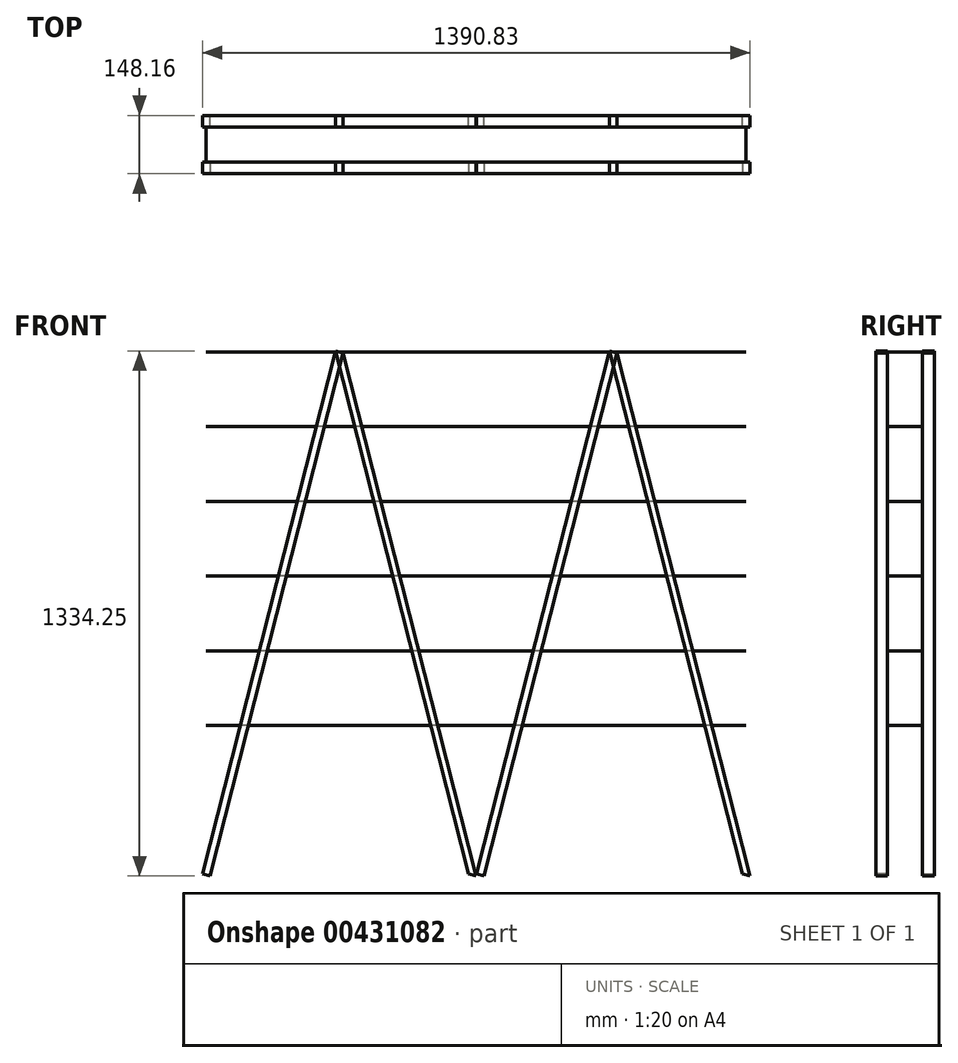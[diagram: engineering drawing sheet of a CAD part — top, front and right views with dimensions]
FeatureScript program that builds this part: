
annotation { "Feature Type Name" : "Feature", "Feature Type Description" : "" }
export const myFeature = defineFeature(function(context is Context, id is Id, definition is map)
    precondition{}
    {
        {
            var Q0;
            Q0=qCreatedBy(makeId("Front.planeOp"),FACE);
            var sketch = newSketch(context, id + "F0", { "sketchPlane" : qUnion([Q0])});
            skLineSegment(sketch, "E0", {"start": v(-53, 736.07) * mm, "end": v(-390.73, -593.3) * mm});
            skLineSegment(sketch, "E1", {"start": v(-53, 736.07) * mm, "end": v(284.75, -593.3) * mm});
            skLineSegment(sketch, "E2", {"start": v(284.75, -593.3) * mm, "end": v(305.39, -593.3) * mm});
            skLineSegment(sketch, "E3", {"start": v(305.39, -593.3) * mm, "end": v(643.13, 736.07) * mm});
            skLineSegment(sketch, "E4", {"start": v(643.13, 736.07) * mm, "end": v(980.87, -593.3) * mm});
            skLineSegment(sketch, "E5", {"start": v(-390.73, -593.3) * mm, "end": v(980.87, -593.3) * mm, "construction": true});
            skLineSegment(sketch, "E6", {"start": v(-390.73, -593.3) * mm, "end": v(-390.73, -645.75) * mm, "construction": true});
            skLineSegment(sketch, "E7", {"start": v(284.75, -593.3) * mm, "end": v(284.75, -645.75) * mm, "construction": true});
            skLineSegment(sketch, "E8", {"start": v(305.39, -593.3) * mm, "end": v(305.39, -645.75) * mm, "construction": true});
            skLineSegment(sketch, "E9", {"start": v(980.87, -593.3) * mm, "end": v(980.87, -645.75) * mm, "construction": true});
            skLineSegment(sketch, "E10", {"start": v(-390.73, -645.75) * mm, "end": v(284.75, -645.75) * mm, "construction": true});
            skLineSegment(sketch, "E11", {"start": v(305.39, -645.75) * mm, "end": v(980.87, -645.75) * mm, "construction": true});
            skLineSegment(sketch, "E12", {"start": v(980.87, 736.07) * mm, "end": v(-390.73, 736.07) * mm});
            skLineSegment(sketch, "E13", {"start": v(980.87, 546.16) * mm, "end": v(-390.73, 546.16) * mm});
            skLineSegment(sketch, "E14", {"start": v(980.87, 356.25) * mm, "end": v(-390.73, 356.25) * mm});
            skLineSegment(sketch, "E15", {"start": v(980.87, 166.34) * mm, "end": v(-390.73, 166.34) * mm});
            skLineSegment(sketch, "E16", {"start": v(980.87, -23.57) * mm, "end": v(-390.73, -23.57) * mm});
            skLineSegment(sketch, "E17", {"start": v(980.87, -213.48) * mm, "end": v(-390.73, -213.48) * mm});
            skLineSegment(sketch, "E18", {"start": v(643.13, 736.07) * mm, "end": v(643.13, 546.16) * mm, "construction": true});
            skLineSegment(sketch, "E19", {"start": v(643.13, 546.16) * mm, "end": v(643.13, 356.25) * mm, "construction": true});
            skLineSegment(sketch, "E20", {"start": v(643.13, 356.25) * mm, "end": v(643.13, 166.34) * mm, "construction": true});
            skLineSegment(sketch, "E21", {"start": v(643.13, 166.34) * mm, "end": v(643.13, -23.57) * mm, "construction": true});
            skLineSegment(sketch, "E22", {"start": v(643.13, -23.57) * mm, "end": v(643.13, -213.48) * mm, "construction": true});
            skLineSegment(sketch, "E23", {"start": v(980.87, -403.4) * mm, "end": v(-390.73, -403.4) * mm, "construction": true});
            skLineSegment(sketch, "E24", {"start": v(643.13, -213.48) * mm, "end": v(643.13, -403.4) * mm});
            skLineSegment(sketch, "E25", {"start": v(643.13, -403.4) * mm, "end": v(643.13, -593.3) * mm});
            skSolve(sketch);
        }
        {
            var Q0;
            Q0=sQuery(id+"F0.wireOp",EDGE,"E12");
            var Q1;
            Q1=sQuery(id+"F0.wireOp",EDGE,"E13");
            var Q2;
            Q2=sQuery(id+"F0.wireOp",EDGE,"E14");
            var Q3;
            Q3=sQuery(id+"F0.wireOp",EDGE,"E15");
            var Q4;
            Q4=sQuery(id+"F0.wireOp",EDGE,"E16");
            var Q5;
            Q5=sQuery(id+"F0.wireOp",EDGE,"E17");
            extrude(context, id + "F1", {"bodyType" : ToolBodyType.SURFACE, "surfaceEntities" : qUnion([Q0, Q1, Q2, Q3, Q4, Q5]), "depth" : 88.9 * mm});
        }
        {
            var Q0;
            Q0=makeQuery(id+"F1.opExtrude","SWEPT_FACE",FACE,{"disambiguationData":[OSD([sQuery(id+"F0.wireOp",EDGE,"E17")])]});
            var Q1;
            Q1=makeQuery(id+"F1.opExtrude","SWEPT_FACE",FACE,{"disambiguationData":[OSD([sQuery(id+"F0.wireOp",EDGE,"E16")])]});
            var Q2;
            Q2=makeQuery(id+"F1.opExtrude","SWEPT_FACE",FACE,{"disambiguationData":[OSD([sQuery(id+"F0.wireOp",EDGE,"E15")])]});
            var Q3;
            Q3=makeQuery(id+"F1.opExtrude","SWEPT_FACE",FACE,{"disambiguationData":[OSD([sQuery(id+"F0.wireOp",EDGE,"E14")])]});
            var Q4;
            Q4=makeQuery(id+"F1.opExtrude","SWEPT_FACE",FACE,{"disambiguationData":[OSD([sQuery(id+"F0.wireOp",EDGE,"E13")])]});
            var Q5;
            Q5=makeQuery(id+"F1.opExtrude","SWEPT_FACE",FACE,{"disambiguationData":[OSD([sQuery(id+"F0.wireOp",EDGE,"E12")])]});
            extrude(context, id + "F2", {"entities" : qUnion([Q0, Q1, Q2, Q3, Q4, Q5]), "depth" : 23 / 1625.6 * mm, "hasSecondDirection" : true, "secondDirectionOppositeDirection" : true, "secondDirectionDepth" : 23 / 1625.6 * mm});
        }
        {
            var Q0;
            Q0=sQuery(id+"F0.wireOp",EDGE,"E0");
            var Q1;
            Q1=sQuery(id+"F0.wireOp",EDGE,"E1");
            var Q2;
            Q2=sQuery(id+"F0.wireOp",EDGE,"E3");
            var Q3;
            Q3=sQuery(id+"F0.wireOp",EDGE,"E4");
            extrude(context, id + "F3", {"bodyType" : ToolBodyType.SURFACE, "surfaceEntities" : qUnion([Q0, Q1, Q2, Q3]), "depth" : -88.9 * mm / 3});
        }
        {
            var Q0;
            Q0=makeQuery(id+"F3.opExtrude","SWEPT_FACE",FACE,{"disambiguationData":[OSD([sQuery(id+"F0.wireOp",EDGE,"E0")])]});
            var Q1;
            Q1=makeQuery(id+"F3.opExtrude","SWEPT_FACE",FACE,{"disambiguationData":[OSD([sQuery(id+"F0.wireOp",EDGE,"E1")])]});
            var Q2;
            Q2=makeQuery(id+"F3.opExtrude","SWEPT_FACE",FACE,{"disambiguationData":[OSD([sQuery(id+"F0.wireOp",EDGE,"E3")])]});
            var Q3;
            Q3=makeQuery(id+"F3.opExtrude","SWEPT_FACE",FACE,{"disambiguationData":[OSD([sQuery(id+"F0.wireOp",EDGE,"E4")])]});
            extrude(context, id + "F4", {"entities" : qUnion([Q0, Q1, Q2, Q3]), "depth" : 9.92 * mm, "hasSecondDirection" : true, "secondDirectionOppositeDirection" : true, "secondDirectionDepth" : 9.92 * mm});
        }
        {
            var Q0;
            {var subQ0=sQuery(id+"F0.wireOp",EDGE,"E15");Q0=makeQuery(id+"F2.opExtrude","SWEPT_FACE",FACE,{"disambiguationData":[OSD([subQ0]),TDD([makeQuery(id+"F1.opExtrude","CAP_EDGE",EDGE,{"disambiguationData":[OSD([subQ0])],"isStart":false})])]});}
            var Q1;
            {var subQ0=sQuery(id+"F0.wireOp",EDGE,"E15");Q1=makeQuery(id+"F2.opExtrude","SWEPT_FACE",FACE,{"disambiguationData":[OSD([subQ0]),TDD([makeQuery(id+"F1.opExtrude","CAP_EDGE",EDGE,{"disambiguationData":[OSD([subQ0])],"isStart":true})])]});}
            cPlane(context, id + "F5", {"entities" : qUnion([Q0, Q1]), "cplaneType" : CPlaneType.MID_PLANE, "offset" : 25.4 * mm, "width" : 152.4 * mm, "height" : 152.4 * mm});
        }
        {
            var Q0;
            Q0=makeQuery(id+"F4.opExtrude","SWEPT_BODY",BODY,{"disambiguationData":[OSD([sQuery(id+"F0.wireOp",EDGE,"E4")])]});
            var Q1;
            Q1=makeQuery(id+"F4.opExtrude","SWEPT_BODY",BODY,{"disambiguationData":[OSD([sQuery(id+"F0.wireOp",EDGE,"E3")])]});
            var Q2;
            Q2=makeQuery(id+"F4.opExtrude","SWEPT_BODY",BODY,{"disambiguationData":[OSD([sQuery(id+"F0.wireOp",EDGE,"E1")])]});
            var Q3;
            Q3=makeQuery(id+"F4.opExtrude","SWEPT_BODY",BODY,{"disambiguationData":[OSD([sQuery(id+"F0.wireOp",EDGE,"E0")])]});
            var Q4;
            Q4=qCreatedBy(id+"F5.planeOp",FACE);
            mirror(context, id + "F6", {"entities" : qUnion([Q0, Q1, Q2, Q3]), "mirrorPlane" : qUnion([Q4])});
        }
    });
